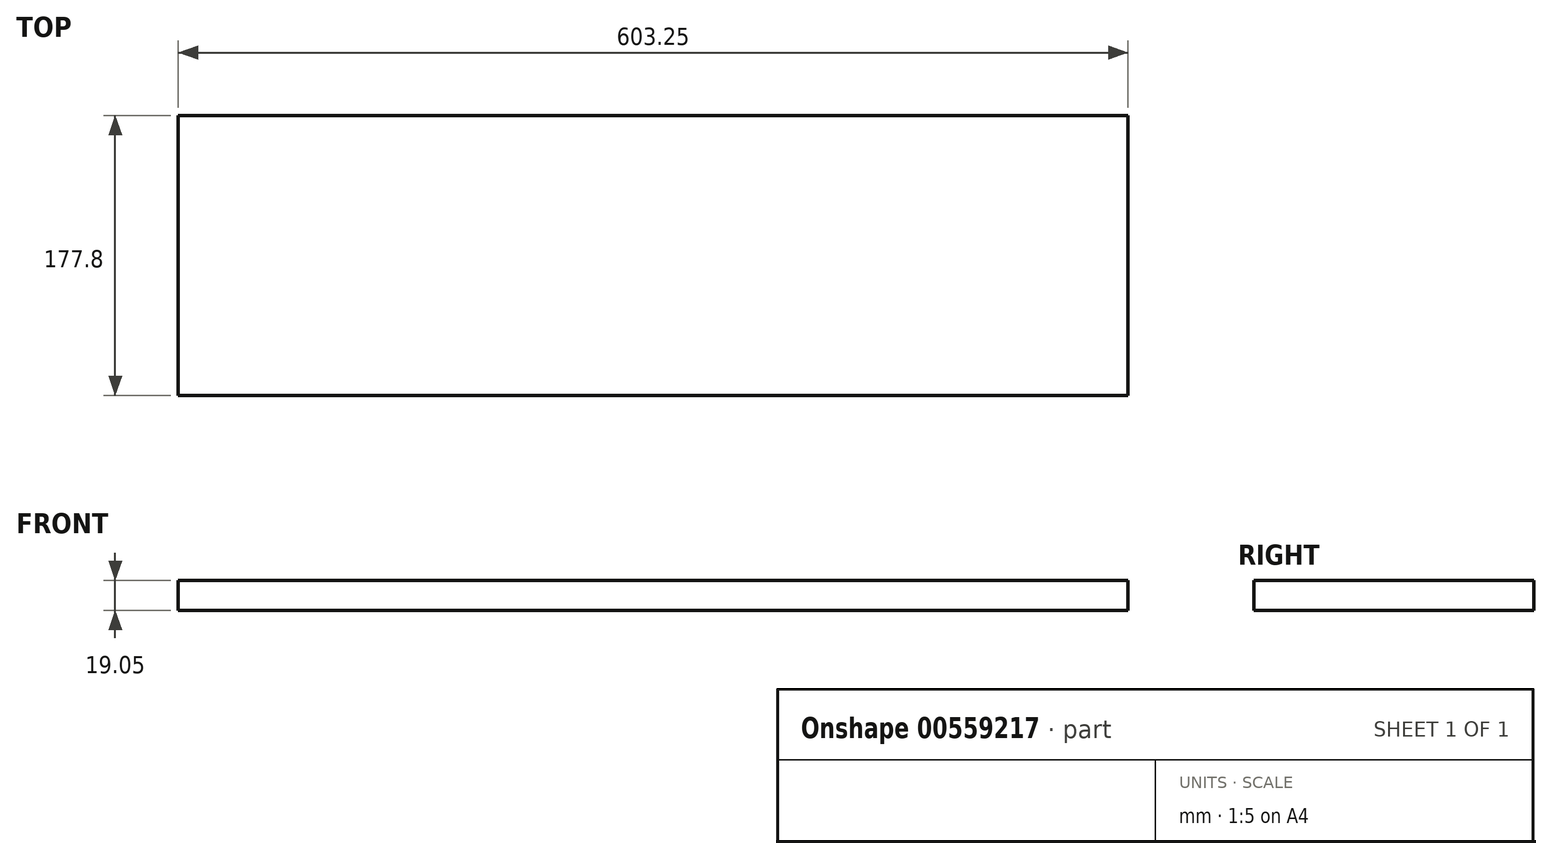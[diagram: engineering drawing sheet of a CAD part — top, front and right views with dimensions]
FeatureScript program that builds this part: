
annotation { "Feature Type Name" : "Feature", "Feature Type Description" : "" }
export const myFeature = defineFeature(function(context is Context, id is Id, definition is map)
    precondition{}
    {
        {
            var Q0;
            Q0=qCreatedBy(makeId("Top.planeOp"),FACE);
            var sketch = newSketch(context, id + "F0", { "sketchPlane" : qUnion([Q0])});
            skLineSegment(sketch, "E0.bottom", {"start": v(0, 0) * mm, "end": v(603.25, 0) * mm});
            skLineSegment(sketch, "E0.top", {"start": v(0, 177.8) * mm, "end": v(603.25, 177.8) * mm});
            skLineSegment(sketch, "E0.left", {"start": v(0, 0) * mm, "end": v(0, 177.8) * mm});
            skLineSegment(sketch, "E0.right", {"start": v(603.25, 0) * mm, "end": v(603.25, 177.8) * mm});
            skSolve(sketch);
        }
        {
            var Q0;
            Q0=makeQuery(id+"F0.imprint","IMPRINT",FACE,{"disambiguationData":[TD([[makeQuery(id+"F0.imprint","IMPRINT",EDGE,{"derivedFrom":sQuery(id+"F0.wireOp",EDGE,"E0.bottom")}),1.0]])]});
            extrude(context, id + "F1", {"entities" : qUnion([Q0]), "depth" : 19.05 * mm, "offsetDistance" : 25.4 * mm});
        }
    });
